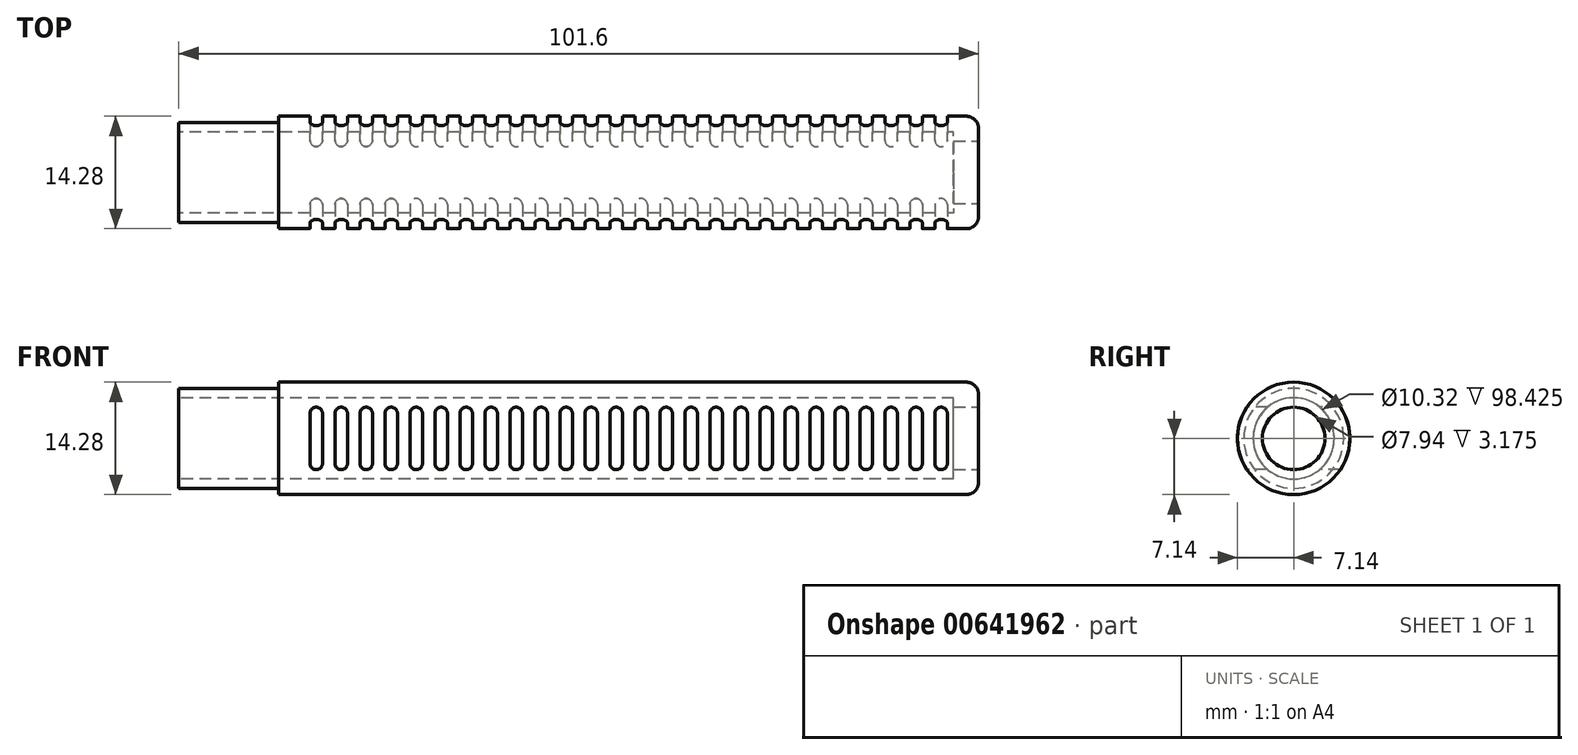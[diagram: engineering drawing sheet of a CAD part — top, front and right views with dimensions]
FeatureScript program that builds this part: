
annotation { "Feature Type Name" : "Feature", "Feature Type Description" : "" }
export const myFeature = defineFeature(function(context is Context, id is Id, definition is map)
    precondition{}
    {
        {
            var Q0;
            Q0=qCreatedBy(makeId("Right.planeOp"),FACE);
            var sketch = newSketch(context, id + "F0", { "sketchPlane" : qUnion([Q0])});
            skCircle(sketch, "E0", {"center": v(0, 0) * mm, "radius": 7.14 * mm});
            skSolve(sketch);
        }
        {
            var Q0;
            Q0=makeQuery(id+"F0.imprint","IMPRINT",FACE,{"disambiguationData":[TD([[makeQuery(id+"F0.imprint","IMPRINT",EDGE,{"derivedFrom":sQuery(id+"F0.wireOp",EDGE,"E0")}),1.0]])]});
            extrude(context, id + "F1", {"entities" : qUnion([Q0]), "depth" : 101.6 * mm, "offsetDistance" : 25.4 * mm});
        }
        {
            var Q0;
            Q0=qCreatedBy(makeId("Right.planeOp"),FACE);
            var sketch = newSketch(context, id + "F2", { "sketchPlane" : qUnion([Q0])});
            skPoint(sketch, "E1", {"position": v(0, 0) * mm});
            skSolve(sketch);
        }
        {
            var Q0;
            Q0=sQuery(id+"F2.wireOp",VERTEX,"E1");
            var Q1;
            Q1=makeQuery(id+"F1.opExtrude","SWEPT_BODY",BODY,{"disambiguationData":[OSD([sQuery(id+"F0.wireOp",EDGE,"E0")])]});
            hole(context, id + "F3", {"style" : HoleStyle.SIMPLE, "endStyle" : HoleEndStyle.THROUGH, "oppositeDirection" : true, "holeDiameter" : 10.32 * mm, "majorDiameter" : 6.35 * mm, "isTappedThrough" : true, "tappedDepth" : 12.7 * mm, "tapClearance" : 3, "locations" : qUnion([Q0]), "scope" : qUnion([Q1])});
        }
        {
            var Q0;
            Q0=qCreatedBy(makeId("Right.planeOp"),FACE);
            var sketch = newSketch(context, id + "F4", { "sketchPlane" : qUnion([Q0])});
            skCircle(sketch, "E2", {"center": v(0, 0) * mm, "radius": 6.35 * mm});
            skCircle(sketch, "E3", {"center": v(0, 0) * mm, "radius": 12.7 * mm});
            skSolve(sketch);
        }
        {
            var Q0;
            Q0=makeQuery(id+"F4.imprint","IMPRINT",FACE,{"disambiguationData":[TD([[makeQuery(id+"F4.imprint","IMPRINT",EDGE,{"derivedFrom":sQuery(id+"F4.wireOp",EDGE,"E2")}),-1.0]])]});
            extrude(context, id + "F5", {"entities" : qUnion([Q0]), "operationType" : NewBodyOperationType.REMOVE, "depth" : 12.7 * mm, "offsetDistance" : 25.4 * mm});
        }
        {
            var Q0;
            Q0=makeQuery(id+"F1.opExtrude","CAP_FACE",FACE,{"disambiguationData":[OSD([sQuery(id+"F0.wireOp",EDGE,"E0")])],"isStart":false});
            var sketch = newSketch(context, id + "F6", { "sketchPlane" : qUnion([Q0])});
            skCircle(sketch, "E4", {"center": v(0, 0) * mm, "radius": 3.97 * mm});
            skCircle(sketch, "E5", {"center": v(0, 0) * mm, "radius": 7.14 * mm});
            skSolve(sketch);
        }
        {
            var Q0;
            Q0=makeQuery(id+"F6.imprint","IMPRINT",FACE,{"disambiguationData":[TD([[makeQuery(id+"F6.imprint","IMPRINT",EDGE,{"derivedFrom":sQuery(id+"F6.wireOp",EDGE,"E4")}),-1.0]])]});
            extrude(context, id + "F7", {"entities" : qUnion([Q0]), "operationType" : NewBodyOperationType.ADD, "oppositeDirection" : true, "depth" : 3.17 * mm, "offsetDistance" : 25.4 * mm});
        }
        {
            var Q0;
            Q0=makeQuery(id+"F1.opExtrude","CAP_EDGE",EDGE,{"disambiguationData":[OSD([sQuery(id+"F0.wireOp",EDGE,"E0")])],"isStart":false});
            fillet(context, id + "F8", {"entities" : qUnion([Q0]), "radius" : 1.59 * mm, "tangentPropagation" : true, "allowEdgeOverflow" : false});
        }
        {
            var Q0;
            Q0=qCreatedBy(makeId("Front.planeOp"),FACE);
            var sketch = newSketch(context, id + "F9", { "sketchPlane" : qUnion([Q0])});
            skLineSegment(sketch, "E6.bottom", {"start": v(96.84, -3.97) * mm, "end": v(96.84, -3.97) * mm});
            skLineSegment(sketch, "E6.top", {"start": v(96.84, 3.97) * mm, "end": v(96.84, 3.97) * mm});
            skLineSegment(sketch, "E6.left", {"start": v(96.04, -3.18) * mm, "end": v(96.04, 3.17) * mm});
            skLineSegment(sketch, "E6.right", {"start": v(97.63, -3.17) * mm, "end": v(97.63, 3.18) * mm});
            skPoint(sketch, "E6.middle", {"position": v(96.84, 0) * mm});
            skPoint(sketch, "E7.visualSharp", {"position": v(96.04, 3.97) * mm});
            skArc(sketch, "E7.filletArc", {"start": v(96.84, 3.97) * mm, "mid": v(96.28, 3.74) * mm, "end": v(96.04, 3.17) * mm});
            skPoint(sketch, "E8.visualSharp", {"position": v(97.63, 3.97) * mm});
            skArc(sketch, "E8.filletArc", {"start": v(97.63, 3.18) * mm, "mid": v(97.4, 3.74) * mm, "end": v(96.84, 3.97) * mm});
            skPoint(sketch, "E9.visualSharp", {"position": v(96.04, -3.97) * mm});
            skArc(sketch, "E9.filletArc", {"start": v(96.04, -3.18) * mm, "mid": v(96.28, -3.74) * mm, "end": v(96.84, -3.97) * mm});
            skPoint(sketch, "E10.visualSharp", {"position": v(97.63, -3.97) * mm});
            skArc(sketch, "E10.filletArc", {"start": v(96.84, -3.97) * mm, "mid": v(97.4, -3.74) * mm, "end": v(97.63, -3.17) * mm});
            skLineSegment(sketch, "E11.1.0.0", {"start": v(93.66, -3.97) * mm, "end": v(93.66, -3.97) * mm});
            skPoint(sketch, "E11.1.0.1", {"position": v(94.46, 3.97) * mm});
            skLineSegment(sketch, "E11.1.0.2", {"start": v(93.66, 3.97) * mm, "end": v(93.66, 3.97) * mm});
            skLineSegment(sketch, "E11.1.0.3", {"start": v(92.87, -3.18) * mm, "end": v(92.87, 3.17) * mm});
            skLineSegment(sketch, "E11.1.0.4", {"start": v(94.46, -3.17) * mm, "end": v(94.46, 3.18) * mm});
            skArc(sketch, "E11.1.0.5", {"start": v(93.66, 3.97) * mm, "mid": v(93.1, 3.74) * mm, "end": v(92.87, 3.17) * mm});
            skArc(sketch, "E11.1.0.6", {"start": v(94.46, 3.18) * mm, "mid": v(94.22, 3.74) * mm, "end": v(93.66, 3.97) * mm});
            skArc(sketch, "E11.1.0.7", {"start": v(93.66, -3.97) * mm, "mid": v(94.22, -3.74) * mm, "end": v(94.46, -3.17) * mm});
            skPoint(sketch, "E11.1.0.8", {"position": v(94.46, -3.97) * mm});
            skArc(sketch, "E11.1.0.9", {"start": v(92.87, -3.18) * mm, "mid": v(93.1, -3.74) * mm, "end": v(93.66, -3.97) * mm});
            skPoint(sketch, "E11.1.0.10", {"position": v(92.87, 3.97) * mm});
            skPoint(sketch, "E11.1.0.11", {"position": v(93.66, 0) * mm});
            skPoint(sketch, "E11.1.0.12", {"position": v(92.87, -3.97) * mm});
            skLineSegment(sketch, "E11.2.0.0", {"start": v(90.49, -3.97) * mm, "end": v(90.49, -3.97) * mm});
            skPoint(sketch, "E11.2.0.1", {"position": v(91.28, 3.97) * mm});
            skLineSegment(sketch, "E11.2.0.2", {"start": v(90.49, 3.97) * mm, "end": v(90.49, 3.97) * mm});
            skLineSegment(sketch, "E11.2.0.3", {"start": v(89.7, -3.18) * mm, "end": v(89.7, 3.17) * mm});
            skLineSegment(sketch, "E11.2.0.4", {"start": v(91.28, -3.17) * mm, "end": v(91.28, 3.18) * mm});
            skArc(sketch, "E11.2.0.5", {"start": v(90.49, 3.97) * mm, "mid": v(89.93, 3.74) * mm, "end": v(89.7, 3.17) * mm});
            skArc(sketch, "E11.2.0.6", {"start": v(91.28, 3.18) * mm, "mid": v(91.05, 3.74) * mm, "end": v(90.49, 3.97) * mm});
            skArc(sketch, "E11.2.0.7", {"start": v(90.49, -3.97) * mm, "mid": v(91.05, -3.74) * mm, "end": v(91.28, -3.17) * mm});
            skPoint(sketch, "E11.2.0.8", {"position": v(91.28, -3.97) * mm});
            skArc(sketch, "E11.2.0.9", {"start": v(89.7, -3.18) * mm, "mid": v(89.93, -3.74) * mm, "end": v(90.49, -3.97) * mm});
            skPoint(sketch, "E11.2.0.10", {"position": v(89.7, 3.97) * mm});
            skPoint(sketch, "E11.2.0.11", {"position": v(90.49, 0) * mm});
            skPoint(sketch, "E11.2.0.12", {"position": v(89.7, -3.97) * mm});
            skLineSegment(sketch, "E11.3.0.0", {"start": v(87.31, -3.97) * mm, "end": v(87.31, -3.97) * mm});
            skPoint(sketch, "E11.3.0.1", {"position": v(88.1, 3.97) * mm});
            skLineSegment(sketch, "E11.3.0.2", {"start": v(87.31, 3.97) * mm, "end": v(87.31, 3.97) * mm});
            skLineSegment(sketch, "E11.3.0.3", {"start": v(86.52, -3.18) * mm, "end": v(86.52, 3.17) * mm});
            skLineSegment(sketch, "E11.3.0.4", {"start": v(88.1, -3.17) * mm, "end": v(88.1, 3.18) * mm});
            skArc(sketch, "E11.3.0.5", {"start": v(87.31, 3.97) * mm, "mid": v(86.75, 3.74) * mm, "end": v(86.52, 3.17) * mm});
            skArc(sketch, "E11.3.0.6", {"start": v(88.1, 3.18) * mm, "mid": v(87.87, 3.74) * mm, "end": v(87.31, 3.97) * mm});
            skArc(sketch, "E11.3.0.7", {"start": v(87.31, -3.97) * mm, "mid": v(87.87, -3.74) * mm, "end": v(88.1, -3.17) * mm});
            skPoint(sketch, "E11.3.0.8", {"position": v(88.1, -3.97) * mm});
            skArc(sketch, "E11.3.0.9", {"start": v(86.52, -3.18) * mm, "mid": v(86.75, -3.74) * mm, "end": v(87.31, -3.97) * mm});
            skPoint(sketch, "E11.3.0.10", {"position": v(86.52, 3.97) * mm});
            skPoint(sketch, "E11.3.0.11", {"position": v(87.31, 0) * mm});
            skPoint(sketch, "E11.3.0.12", {"position": v(86.52, -3.97) * mm});
            skLineSegment(sketch, "E11.4.0.0", {"start": v(84.14, -3.97) * mm, "end": v(84.14, -3.97) * mm});
            skPoint(sketch, "E11.4.0.1", {"position": v(84.93, 3.97) * mm});
            skLineSegment(sketch, "E11.4.0.2", {"start": v(84.14, 3.97) * mm, "end": v(84.14, 3.97) * mm});
            skLineSegment(sketch, "E11.4.0.3", {"start": v(83.34, -3.18) * mm, "end": v(83.34, 3.17) * mm});
            skLineSegment(sketch, "E11.4.0.4", {"start": v(84.93, -3.17) * mm, "end": v(84.93, 3.18) * mm});
            skArc(sketch, "E11.4.0.5", {"start": v(84.14, 3.97) * mm, "mid": v(83.58, 3.74) * mm, "end": v(83.34, 3.17) * mm});
            skArc(sketch, "E11.4.0.6", {"start": v(84.93, 3.18) * mm, "mid": v(84.7, 3.74) * mm, "end": v(84.14, 3.97) * mm});
            skArc(sketch, "E11.4.0.7", {"start": v(84.14, -3.97) * mm, "mid": v(84.7, -3.74) * mm, "end": v(84.93, -3.17) * mm});
            skPoint(sketch, "E11.4.0.8", {"position": v(84.93, -3.97) * mm});
            skArc(sketch, "E11.4.0.9", {"start": v(83.34, -3.18) * mm, "mid": v(83.58, -3.74) * mm, "end": v(84.14, -3.97) * mm});
            skPoint(sketch, "E11.4.0.10", {"position": v(83.34, 3.97) * mm});
            skPoint(sketch, "E11.4.0.11", {"position": v(84.14, 0) * mm});
            skPoint(sketch, "E11.4.0.12", {"position": v(83.34, -3.97) * mm});
            skLineSegment(sketch, "E11.5.0.0", {"start": v(80.96, -3.97) * mm, "end": v(80.96, -3.97) * mm});
            skPoint(sketch, "E11.5.0.1", {"position": v(81.76, 3.97) * mm});
            skLineSegment(sketch, "E11.5.0.2", {"start": v(80.96, 3.97) * mm, "end": v(80.96, 3.97) * mm});
            skLineSegment(sketch, "E11.5.0.3", {"start": v(80.17, -3.18) * mm, "end": v(80.17, 3.17) * mm});
            skLineSegment(sketch, "E11.5.0.4", {"start": v(81.76, -3.17) * mm, "end": v(81.76, 3.18) * mm});
            skArc(sketch, "E11.5.0.5", {"start": v(80.96, 3.97) * mm, "mid": v(80.4, 3.74) * mm, "end": v(80.17, 3.17) * mm});
            skArc(sketch, "E11.5.0.6", {"start": v(81.76, 3.18) * mm, "mid": v(81.52, 3.74) * mm, "end": v(80.96, 3.97) * mm});
            skArc(sketch, "E11.5.0.7", {"start": v(80.96, -3.97) * mm, "mid": v(81.52, -3.74) * mm, "end": v(81.76, -3.17) * mm});
            skPoint(sketch, "E11.5.0.8", {"position": v(81.76, -3.97) * mm});
            skArc(sketch, "E11.5.0.9", {"start": v(80.17, -3.18) * mm, "mid": v(80.4, -3.74) * mm, "end": v(80.96, -3.97) * mm});
            skPoint(sketch, "E11.5.0.10", {"position": v(80.17, 3.97) * mm});
            skPoint(sketch, "E11.5.0.11", {"position": v(80.96, 0) * mm});
            skPoint(sketch, "E11.5.0.12", {"position": v(80.17, -3.97) * mm});
            skLineSegment(sketch, "E11.6.0.0", {"start": v(77.79, -3.97) * mm, "end": v(77.79, -3.97) * mm});
            skPoint(sketch, "E11.6.0.1", {"position": v(78.58, 3.97) * mm});
            skLineSegment(sketch, "E11.6.0.2", {"start": v(77.79, 3.97) * mm, "end": v(77.79, 3.97) * mm});
            skLineSegment(sketch, "E11.6.0.3", {"start": v(77, -3.18) * mm, "end": v(77, 3.17) * mm});
            skLineSegment(sketch, "E11.6.0.4", {"start": v(78.58, -3.17) * mm, "end": v(78.58, 3.18) * mm});
            skArc(sketch, "E11.6.0.5", {"start": v(77.79, 3.97) * mm, "mid": v(77.23, 3.74) * mm, "end": v(77, 3.17) * mm});
            skArc(sketch, "E11.6.0.6", {"start": v(78.58, 3.18) * mm, "mid": v(78.35, 3.74) * mm, "end": v(77.79, 3.97) * mm});
            skArc(sketch, "E11.6.0.7", {"start": v(77.79, -3.97) * mm, "mid": v(78.35, -3.74) * mm, "end": v(78.58, -3.17) * mm});
            skPoint(sketch, "E11.6.0.8", {"position": v(78.58, -3.97) * mm});
            skArc(sketch, "E11.6.0.9", {"start": v(77, -3.18) * mm, "mid": v(77.23, -3.74) * mm, "end": v(77.79, -3.97) * mm});
            skPoint(sketch, "E11.6.0.10", {"position": v(77, 3.97) * mm});
            skPoint(sketch, "E11.6.0.11", {"position": v(77.79, 0) * mm});
            skPoint(sketch, "E11.6.0.12", {"position": v(77, -3.97) * mm});
            skLineSegment(sketch, "E11.7.0.0", {"start": v(74.61, -3.97) * mm, "end": v(74.61, -3.97) * mm});
            skPoint(sketch, "E11.7.0.1", {"position": v(75.4, 3.97) * mm});
            skLineSegment(sketch, "E11.7.0.2", {"start": v(74.61, 3.97) * mm, "end": v(74.61, 3.97) * mm});
            skLineSegment(sketch, "E11.7.0.3", {"start": v(73.82, -3.18) * mm, "end": v(73.82, 3.17) * mm});
            skLineSegment(sketch, "E11.7.0.4", {"start": v(75.4, -3.17) * mm, "end": v(75.4, 3.18) * mm});
            skArc(sketch, "E11.7.0.5", {"start": v(74.61, 3.97) * mm, "mid": v(74.05, 3.74) * mm, "end": v(73.82, 3.17) * mm});
            skArc(sketch, "E11.7.0.6", {"start": v(75.4, 3.18) * mm, "mid": v(75.17, 3.74) * mm, "end": v(74.61, 3.97) * mm});
            skArc(sketch, "E11.7.0.7", {"start": v(74.61, -3.97) * mm, "mid": v(75.17, -3.74) * mm, "end": v(75.4, -3.17) * mm});
            skPoint(sketch, "E11.7.0.8", {"position": v(75.4, -3.97) * mm});
            skArc(sketch, "E11.7.0.9", {"start": v(73.82, -3.18) * mm, "mid": v(74.05, -3.74) * mm, "end": v(74.61, -3.97) * mm});
            skPoint(sketch, "E11.7.0.10", {"position": v(73.82, 3.97) * mm});
            skPoint(sketch, "E11.7.0.11", {"position": v(74.61, 0) * mm});
            skPoint(sketch, "E11.7.0.12", {"position": v(73.82, -3.97) * mm});
            skLineSegment(sketch, "E11.8.0.0", {"start": v(71.44, -3.97) * mm, "end": v(71.44, -3.97) * mm});
            skPoint(sketch, "E11.8.0.1", {"position": v(72.23, 3.97) * mm});
            skLineSegment(sketch, "E11.8.0.2", {"start": v(71.44, 3.97) * mm, "end": v(71.44, 3.97) * mm});
            skLineSegment(sketch, "E11.8.0.3", {"start": v(70.64, -3.18) * mm, "end": v(70.64, 3.17) * mm});
            skLineSegment(sketch, "E11.8.0.4", {"start": v(72.23, -3.17) * mm, "end": v(72.23, 3.18) * mm});
            skArc(sketch, "E11.8.0.5", {"start": v(71.44, 3.97) * mm, "mid": v(70.88, 3.74) * mm, "end": v(70.64, 3.17) * mm});
            skArc(sketch, "E11.8.0.6", {"start": v(72.23, 3.18) * mm, "mid": v(72, 3.74) * mm, "end": v(71.44, 3.97) * mm});
            skArc(sketch, "E11.8.0.7", {"start": v(71.44, -3.97) * mm, "mid": v(72, -3.74) * mm, "end": v(72.23, -3.17) * mm});
            skPoint(sketch, "E11.8.0.8", {"position": v(72.23, -3.97) * mm});
            skArc(sketch, "E11.8.0.9", {"start": v(70.64, -3.18) * mm, "mid": v(70.88, -3.74) * mm, "end": v(71.44, -3.97) * mm});
            skPoint(sketch, "E11.8.0.10", {"position": v(70.64, 3.97) * mm});
            skPoint(sketch, "E11.8.0.11", {"position": v(71.44, 0) * mm});
            skPoint(sketch, "E11.8.0.12", {"position": v(70.64, -3.97) * mm});
            skLineSegment(sketch, "E11.9.0.0", {"start": v(68.26, -3.97) * mm, "end": v(68.26, -3.97) * mm});
            skPoint(sketch, "E11.9.0.1", {"position": v(69.06, 3.97) * mm});
            skLineSegment(sketch, "E11.9.0.2", {"start": v(68.26, 3.97) * mm, "end": v(68.26, 3.97) * mm});
            skLineSegment(sketch, "E11.9.0.3", {"start": v(67.47, -3.18) * mm, "end": v(67.47, 3.17) * mm});
            skLineSegment(sketch, "E11.9.0.4", {"start": v(69.06, -3.17) * mm, "end": v(69.06, 3.17) * mm});
            skArc(sketch, "E11.9.0.5", {"start": v(68.26, 3.97) * mm, "mid": v(67.7, 3.74) * mm, "end": v(67.47, 3.17) * mm});
            skArc(sketch, "E11.9.0.6", {"start": v(69.06, 3.17) * mm, "mid": v(68.82, 3.74) * mm, "end": v(68.26, 3.97) * mm});
            skArc(sketch, "E11.9.0.7", {"start": v(68.26, -3.97) * mm, "mid": v(68.82, -3.74) * mm, "end": v(69.06, -3.17) * mm});
            skPoint(sketch, "E11.9.0.8", {"position": v(69.06, -3.97) * mm});
            skArc(sketch, "E11.9.0.9", {"start": v(67.47, -3.18) * mm, "mid": v(67.7, -3.74) * mm, "end": v(68.26, -3.97) * mm});
            skPoint(sketch, "E11.9.0.10", {"position": v(67.47, 3.97) * mm});
            skPoint(sketch, "E11.9.0.11", {"position": v(68.26, 0) * mm});
            skPoint(sketch, "E11.9.0.12", {"position": v(67.47, -3.97) * mm});
            skLineSegment(sketch, "E11.10.0.0", {"start": v(65.09, -3.97) * mm, "end": v(65.09, -3.97) * mm});
            skPoint(sketch, "E11.10.0.1", {"position": v(65.88, 3.97) * mm});
            skLineSegment(sketch, "E11.10.0.2", {"start": v(65.09, 3.97) * mm, "end": v(65.09, 3.97) * mm});
            skLineSegment(sketch, "E11.10.0.3", {"start": v(64.3, -3.18) * mm, "end": v(64.3, 3.17) * mm});
            skLineSegment(sketch, "E11.10.0.4", {"start": v(65.88, -3.17) * mm, "end": v(65.88, 3.17) * mm});
            skArc(sketch, "E11.10.0.5", {"start": v(65.09, 3.97) * mm, "mid": v(64.53, 3.74) * mm, "end": v(64.3, 3.17) * mm});
            skArc(sketch, "E11.10.0.6", {"start": v(65.88, 3.17) * mm, "mid": v(65.65, 3.74) * mm, "end": v(65.09, 3.97) * mm});
            skArc(sketch, "E11.10.0.7", {"start": v(65.09, -3.97) * mm, "mid": v(65.65, -3.74) * mm, "end": v(65.88, -3.17) * mm});
            skPoint(sketch, "E11.10.0.8", {"position": v(65.88, -3.97) * mm});
            skArc(sketch, "E11.10.0.9", {"start": v(64.3, -3.18) * mm, "mid": v(64.53, -3.74) * mm, "end": v(65.09, -3.97) * mm});
            skPoint(sketch, "E11.10.0.10", {"position": v(64.3, 3.97) * mm});
            skPoint(sketch, "E11.10.0.11", {"position": v(65.09, 0) * mm});
            skPoint(sketch, "E11.10.0.12", {"position": v(64.3, -3.97) * mm});
            skLineSegment(sketch, "E11.11.0.0", {"start": v(61.91, -3.97) * mm, "end": v(61.91, -3.97) * mm});
            skPoint(sketch, "E11.11.0.1", {"position": v(62.7, 3.97) * mm});
            skLineSegment(sketch, "E11.11.0.2", {"start": v(61.91, 3.97) * mm, "end": v(61.91, 3.97) * mm});
            skLineSegment(sketch, "E11.11.0.3", {"start": v(61.12, -3.18) * mm, "end": v(61.12, 3.17) * mm});
            skLineSegment(sketch, "E11.11.0.4", {"start": v(62.7, -3.17) * mm, "end": v(62.7, 3.17) * mm});
            skArc(sketch, "E11.11.0.5", {"start": v(61.91, 3.97) * mm, "mid": v(61.35, 3.74) * mm, "end": v(61.12, 3.17) * mm});
            skArc(sketch, "E11.11.0.6", {"start": v(62.7, 3.17) * mm, "mid": v(62.47, 3.74) * mm, "end": v(61.91, 3.97) * mm});
            skArc(sketch, "E11.11.0.7", {"start": v(61.91, -3.97) * mm, "mid": v(62.47, -3.74) * mm, "end": v(62.7, -3.17) * mm});
            skPoint(sketch, "E11.11.0.8", {"position": v(62.7, -3.97) * mm});
            skArc(sketch, "E11.11.0.9", {"start": v(61.12, -3.18) * mm, "mid": v(61.35, -3.74) * mm, "end": v(61.91, -3.97) * mm});
            skPoint(sketch, "E11.11.0.10", {"position": v(61.12, 3.97) * mm});
            skPoint(sketch, "E11.11.0.11", {"position": v(61.91, 0) * mm});
            skPoint(sketch, "E11.11.0.12", {"position": v(61.12, -3.97) * mm});
            skLineSegment(sketch, "E11.direction1", {"start": v(96.04, -3.97) * mm, "end": v(92.87, -3.97) * mm, "construction": true});
            skLineSegment(sketch, "E12.0.12.0", {"start": v(58.74, -3.97) * mm, "end": v(58.74, -3.97) * mm});
            skPoint(sketch, "E12.3.12.0", {"position": v(59.53, 3.97) * mm});
            skLineSegment(sketch, "E12.4.12.0", {"start": v(58.74, 3.97) * mm, "end": v(58.74, 3.97) * mm});
            skLineSegment(sketch, "E12.7.12.0", {"start": v(57.94, -3.18) * mm, "end": v(57.94, 3.17) * mm});
            skLineSegment(sketch, "E12.10.12.0", {"start": v(59.53, -3.18) * mm, "end": v(59.53, 3.17) * mm});
            skArc(sketch, "E12.13.12.0", {"start": v(58.74, 3.97) * mm, "mid": v(58.18, 3.74) * mm, "end": v(57.94, 3.17) * mm});
            skArc(sketch, "E12.17.12.0", {"start": v(59.53, 3.17) * mm, "mid": v(59.3, 3.74) * mm, "end": v(58.74, 3.97) * mm});
            skArc(sketch, "E12.21.12.0", {"start": v(58.74, -3.97) * mm, "mid": v(59.3, -3.74) * mm, "end": v(59.53, -3.18) * mm});
            skPoint(sketch, "E12.25.12.0", {"position": v(59.53, -3.97) * mm});
            skArc(sketch, "E12.26.12.0", {"start": v(57.94, -3.18) * mm, "mid": v(58.18, -3.74) * mm, "end": v(58.74, -3.97) * mm});
            skPoint(sketch, "E12.30.12.0", {"position": v(57.94, 3.97) * mm});
            skPoint(sketch, "E12.31.12.0", {"position": v(58.74, 0) * mm});
            skPoint(sketch, "E12.32.12.0", {"position": v(57.94, -3.97) * mm});
            skLineSegment(sketch, "E12.0.13.0", {"start": v(55.56, -3.97) * mm, "end": v(55.56, -3.97) * mm});
            skPoint(sketch, "E12.3.13.0", {"position": v(56.36, 3.97) * mm});
            skLineSegment(sketch, "E12.4.13.0", {"start": v(55.56, 3.97) * mm, "end": v(55.56, 3.97) * mm});
            skLineSegment(sketch, "E12.7.13.0", {"start": v(54.77, -3.18) * mm, "end": v(54.77, 3.17) * mm});
            skLineSegment(sketch, "E12.10.13.0", {"start": v(56.36, -3.18) * mm, "end": v(56.36, 3.17) * mm});
            skArc(sketch, "E12.13.13.0", {"start": v(55.56, 3.97) * mm, "mid": v(55, 3.74) * mm, "end": v(54.77, 3.17) * mm});
            skArc(sketch, "E12.17.13.0", {"start": v(56.36, 3.17) * mm, "mid": v(56.12, 3.74) * mm, "end": v(55.56, 3.97) * mm});
            skArc(sketch, "E12.21.13.0", {"start": v(55.56, -3.97) * mm, "mid": v(56.12, -3.74) * mm, "end": v(56.36, -3.18) * mm});
            skPoint(sketch, "E12.25.13.0", {"position": v(56.36, -3.97) * mm});
            skArc(sketch, "E12.26.13.0", {"start": v(54.77, -3.18) * mm, "mid": v(55, -3.74) * mm, "end": v(55.56, -3.97) * mm});
            skPoint(sketch, "E12.30.13.0", {"position": v(54.77, 3.97) * mm});
            skPoint(sketch, "E12.31.13.0", {"position": v(55.56, 0) * mm});
            skPoint(sketch, "E12.32.13.0", {"position": v(54.77, -3.97) * mm});
            skLineSegment(sketch, "E12.0.14.0", {"start": v(52.39, -3.97) * mm, "end": v(52.39, -3.97) * mm});
            skPoint(sketch, "E12.3.14.0", {"position": v(53.18, 3.97) * mm});
            skLineSegment(sketch, "E12.4.14.0", {"start": v(52.39, 3.97) * mm, "end": v(52.39, 3.97) * mm});
            skLineSegment(sketch, "E12.7.14.0", {"start": v(51.6, -3.18) * mm, "end": v(51.6, 3.17) * mm});
            skLineSegment(sketch, "E12.10.14.0", {"start": v(53.18, -3.18) * mm, "end": v(53.18, 3.17) * mm});
            skArc(sketch, "E12.13.14.0", {"start": v(52.39, 3.97) * mm, "mid": v(51.83, 3.74) * mm, "end": v(51.6, 3.17) * mm});
            skArc(sketch, "E12.17.14.0", {"start": v(53.18, 3.17) * mm, "mid": v(52.95, 3.74) * mm, "end": v(52.39, 3.97) * mm});
            skArc(sketch, "E12.21.14.0", {"start": v(52.39, -3.97) * mm, "mid": v(52.95, -3.74) * mm, "end": v(53.18, -3.18) * mm});
            skPoint(sketch, "E12.25.14.0", {"position": v(53.18, -3.97) * mm});
            skArc(sketch, "E12.26.14.0", {"start": v(51.6, -3.18) * mm, "mid": v(51.83, -3.74) * mm, "end": v(52.39, -3.97) * mm});
            skPoint(sketch, "E12.30.14.0", {"position": v(51.6, 3.97) * mm});
            skPoint(sketch, "E12.31.14.0", {"position": v(52.39, 0) * mm});
            skPoint(sketch, "E12.32.14.0", {"position": v(51.6, -3.97) * mm});
            skLineSegment(sketch, "E12.0.15.0", {"start": v(49.21, -3.97) * mm, "end": v(49.21, -3.97) * mm});
            skPoint(sketch, "E12.3.15.0", {"position": v(50, 3.97) * mm});
            skLineSegment(sketch, "E12.4.15.0", {"start": v(49.21, 3.97) * mm, "end": v(49.21, 3.97) * mm});
            skLineSegment(sketch, "E12.7.15.0", {"start": v(48.42, -3.18) * mm, "end": v(48.42, 3.17) * mm});
            skLineSegment(sketch, "E12.10.15.0", {"start": v(50, -3.18) * mm, "end": v(50, 3.17) * mm});
            skArc(sketch, "E12.13.15.0", {"start": v(49.21, 3.97) * mm, "mid": v(48.65, 3.74) * mm, "end": v(48.42, 3.17) * mm});
            skArc(sketch, "E12.17.15.0", {"start": v(50, 3.17) * mm, "mid": v(49.77, 3.74) * mm, "end": v(49.21, 3.97) * mm});
            skArc(sketch, "E12.21.15.0", {"start": v(49.21, -3.97) * mm, "mid": v(49.77, -3.74) * mm, "end": v(50, -3.18) * mm});
            skPoint(sketch, "E12.25.15.0", {"position": v(50, -3.97) * mm});
            skArc(sketch, "E12.26.15.0", {"start": v(48.42, -3.18) * mm, "mid": v(48.65, -3.74) * mm, "end": v(49.21, -3.97) * mm});
            skPoint(sketch, "E12.30.15.0", {"position": v(48.42, 3.97) * mm});
            skPoint(sketch, "E12.31.15.0", {"position": v(49.21, 0) * mm});
            skPoint(sketch, "E12.32.15.0", {"position": v(48.42, -3.97) * mm});
            skLineSegment(sketch, "E13.0.16.0", {"start": v(46.04, -3.97) * mm, "end": v(46.04, -3.97) * mm});
            skPoint(sketch, "E13.3.16.0", {"position": v(46.83, 3.97) * mm});
            skLineSegment(sketch, "E13.4.16.0", {"start": v(46.04, 3.97) * mm, "end": v(46.04, 3.97) * mm});
            skLineSegment(sketch, "E13.7.16.0", {"start": v(45.24, -3.18) * mm, "end": v(45.24, 3.17) * mm});
            skLineSegment(sketch, "E13.10.16.0", {"start": v(46.83, -3.18) * mm, "end": v(46.83, 3.17) * mm});
            skArc(sketch, "E13.13.16.0", {"start": v(46.04, 3.97) * mm, "mid": v(45.48, 3.74) * mm, "end": v(45.24, 3.17) * mm});
            skArc(sketch, "E13.17.16.0", {"start": v(46.83, 3.17) * mm, "mid": v(46.6, 3.74) * mm, "end": v(46.04, 3.97) * mm});
            skArc(sketch, "E13.21.16.0", {"start": v(46.04, -3.97) * mm, "mid": v(46.6, -3.74) * mm, "end": v(46.83, -3.18) * mm});
            skPoint(sketch, "E13.25.16.0", {"position": v(46.83, -3.97) * mm});
            skArc(sketch, "E13.26.16.0", {"start": v(45.24, -3.18) * mm, "mid": v(45.48, -3.74) * mm, "end": v(46.04, -3.97) * mm});
            skPoint(sketch, "E13.30.16.0", {"position": v(45.24, 3.97) * mm});
            skPoint(sketch, "E13.31.16.0", {"position": v(46.04, 0) * mm});
            skPoint(sketch, "E13.32.16.0", {"position": v(45.24, -3.97) * mm});
            skLineSegment(sketch, "E13.0.17.0", {"start": v(42.86, -3.97) * mm, "end": v(42.86, -3.97) * mm});
            skPoint(sketch, "E13.3.17.0", {"position": v(43.66, 3.97) * mm});
            skLineSegment(sketch, "E13.4.17.0", {"start": v(42.86, 3.97) * mm, "end": v(42.86, 3.97) * mm});
            skLineSegment(sketch, "E13.7.17.0", {"start": v(42.07, -3.18) * mm, "end": v(42.07, 3.17) * mm});
            skLineSegment(sketch, "E13.10.17.0", {"start": v(43.66, -3.18) * mm, "end": v(43.66, 3.17) * mm});
            skArc(sketch, "E13.13.17.0", {"start": v(42.86, 3.97) * mm, "mid": v(42.3, 3.74) * mm, "end": v(42.07, 3.17) * mm});
            skArc(sketch, "E13.17.17.0", {"start": v(43.66, 3.17) * mm, "mid": v(43.42, 3.74) * mm, "end": v(42.86, 3.97) * mm});
            skArc(sketch, "E13.21.17.0", {"start": v(42.86, -3.97) * mm, "mid": v(43.42, -3.74) * mm, "end": v(43.66, -3.18) * mm});
            skPoint(sketch, "E13.25.17.0", {"position": v(43.66, -3.97) * mm});
            skArc(sketch, "E13.26.17.0", {"start": v(42.07, -3.18) * mm, "mid": v(42.3, -3.74) * mm, "end": v(42.86, -3.97) * mm});
            skPoint(sketch, "E13.30.17.0", {"position": v(42.07, 3.97) * mm});
            skPoint(sketch, "E13.31.17.0", {"position": v(42.86, 0) * mm});
            skPoint(sketch, "E13.32.17.0", {"position": v(42.07, -3.97) * mm});
            skLineSegment(sketch, "E13.0.18.0", {"start": v(39.69, -3.97) * mm, "end": v(39.69, -3.97) * mm});
            skPoint(sketch, "E13.3.18.0", {"position": v(40.48, 3.97) * mm});
            skLineSegment(sketch, "E13.4.18.0", {"start": v(39.69, 3.97) * mm, "end": v(39.69, 3.97) * mm});
            skLineSegment(sketch, "E13.7.18.0", {"start": v(38.9, -3.18) * mm, "end": v(38.9, 3.17) * mm});
            skLineSegment(sketch, "E13.10.18.0", {"start": v(40.48, -3.18) * mm, "end": v(40.48, 3.17) * mm});
            skArc(sketch, "E13.13.18.0", {"start": v(39.69, 3.97) * mm, "mid": v(39.13, 3.74) * mm, "end": v(38.9, 3.17) * mm});
            skArc(sketch, "E13.17.18.0", {"start": v(40.48, 3.17) * mm, "mid": v(40.25, 3.74) * mm, "end": v(39.69, 3.97) * mm});
            skArc(sketch, "E13.21.18.0", {"start": v(39.69, -3.97) * mm, "mid": v(40.25, -3.74) * mm, "end": v(40.48, -3.18) * mm});
            skPoint(sketch, "E13.25.18.0", {"position": v(40.48, -3.97) * mm});
            skArc(sketch, "E13.26.18.0", {"start": v(38.9, -3.18) * mm, "mid": v(39.13, -3.74) * mm, "end": v(39.69, -3.97) * mm});
            skPoint(sketch, "E13.30.18.0", {"position": v(38.9, 3.97) * mm});
            skPoint(sketch, "E13.31.18.0", {"position": v(39.69, 0) * mm});
            skPoint(sketch, "E13.32.18.0", {"position": v(38.9, -3.97) * mm});
            skLineSegment(sketch, "E13.0.19.0", {"start": v(36.51, -3.97) * mm, "end": v(36.51, -3.97) * mm});
            skPoint(sketch, "E13.3.19.0", {"position": v(37.3, 3.97) * mm});
            skLineSegment(sketch, "E13.4.19.0", {"start": v(36.51, 3.97) * mm, "end": v(36.51, 3.97) * mm});
            skLineSegment(sketch, "E13.7.19.0", {"start": v(35.72, -3.18) * mm, "end": v(35.72, 3.17) * mm});
            skLineSegment(sketch, "E13.10.19.0", {"start": v(37.3, -3.18) * mm, "end": v(37.3, 3.17) * mm});
            skArc(sketch, "E13.13.19.0", {"start": v(36.51, 3.97) * mm, "mid": v(35.95, 3.74) * mm, "end": v(35.72, 3.17) * mm});
            skArc(sketch, "E13.17.19.0", {"start": v(37.3, 3.17) * mm, "mid": v(37.07, 3.74) * mm, "end": v(36.51, 3.97) * mm});
            skArc(sketch, "E13.21.19.0", {"start": v(36.51, -3.97) * mm, "mid": v(37.07, -3.74) * mm, "end": v(37.3, -3.18) * mm});
            skPoint(sketch, "E13.25.19.0", {"position": v(37.3, -3.97) * mm});
            skArc(sketch, "E13.26.19.0", {"start": v(35.72, -3.18) * mm, "mid": v(35.95, -3.74) * mm, "end": v(36.51, -3.97) * mm});
            skPoint(sketch, "E13.30.19.0", {"position": v(35.72, 3.97) * mm});
            skPoint(sketch, "E13.31.19.0", {"position": v(36.51, 0) * mm});
            skPoint(sketch, "E13.32.19.0", {"position": v(35.72, -3.97) * mm});
            skLineSegment(sketch, "E13.0.20.0", {"start": v(33.34, -3.97) * mm, "end": v(33.34, -3.97) * mm});
            skPoint(sketch, "E13.3.20.0", {"position": v(34.13, 3.97) * mm});
            skLineSegment(sketch, "E13.4.20.0", {"start": v(33.34, 3.97) * mm, "end": v(33.34, 3.97) * mm});
            skLineSegment(sketch, "E13.7.20.0", {"start": v(32.54, -3.18) * mm, "end": v(32.54, 3.17) * mm});
            skLineSegment(sketch, "E13.10.20.0", {"start": v(34.13, -3.18) * mm, "end": v(34.13, 3.17) * mm});
            skArc(sketch, "E13.13.20.0", {"start": v(33.34, 3.97) * mm, "mid": v(32.78, 3.74) * mm, "end": v(32.54, 3.17) * mm});
            skArc(sketch, "E13.17.20.0", {"start": v(34.13, 3.17) * mm, "mid": v(33.9, 3.74) * mm, "end": v(33.34, 3.97) * mm});
            skArc(sketch, "E13.21.20.0", {"start": v(33.34, -3.97) * mm, "mid": v(33.9, -3.74) * mm, "end": v(34.13, -3.18) * mm});
            skPoint(sketch, "E13.25.20.0", {"position": v(34.13, -3.97) * mm});
            skArc(sketch, "E13.26.20.0", {"start": v(32.54, -3.18) * mm, "mid": v(32.78, -3.74) * mm, "end": v(33.34, -3.97) * mm});
            skPoint(sketch, "E13.30.20.0", {"position": v(32.54, 3.97) * mm});
            skPoint(sketch, "E13.31.20.0", {"position": v(33.34, 0) * mm});
            skPoint(sketch, "E13.32.20.0", {"position": v(32.54, -3.97) * mm});
            skLineSegment(sketch, "E13.0.21.0", {"start": v(30.16, -3.97) * mm, "end": v(30.16, -3.97) * mm});
            skPoint(sketch, "E13.3.21.0", {"position": v(30.96, 3.97) * mm});
            skLineSegment(sketch, "E13.4.21.0", {"start": v(30.16, 3.97) * mm, "end": v(30.16, 3.97) * mm});
            skLineSegment(sketch, "E13.7.21.0", {"start": v(29.37, -3.18) * mm, "end": v(29.37, 3.17) * mm});
            skLineSegment(sketch, "E13.10.21.0", {"start": v(30.96, -3.18) * mm, "end": v(30.96, 3.17) * mm});
            skArc(sketch, "E13.13.21.0", {"start": v(30.16, 3.97) * mm, "mid": v(29.6, 3.74) * mm, "end": v(29.37, 3.17) * mm});
            skArc(sketch, "E13.17.21.0", {"start": v(30.96, 3.17) * mm, "mid": v(30.72, 3.74) * mm, "end": v(30.16, 3.97) * mm});
            skArc(sketch, "E13.21.21.0", {"start": v(30.16, -3.97) * mm, "mid": v(30.72, -3.74) * mm, "end": v(30.96, -3.18) * mm});
            skPoint(sketch, "E13.25.21.0", {"position": v(30.96, -3.97) * mm});
            skArc(sketch, "E13.26.21.0", {"start": v(29.37, -3.18) * mm, "mid": v(29.6, -3.74) * mm, "end": v(30.16, -3.97) * mm});
            skPoint(sketch, "E13.30.21.0", {"position": v(29.37, 3.97) * mm});
            skPoint(sketch, "E13.31.21.0", {"position": v(30.16, 0) * mm});
            skPoint(sketch, "E13.32.21.0", {"position": v(29.37, -3.97) * mm});
            skLineSegment(sketch, "E13.0.22.0", {"start": v(26.99, -3.97) * mm, "end": v(26.99, -3.97) * mm});
            skPoint(sketch, "E13.3.22.0", {"position": v(27.78, 3.97) * mm});
            skLineSegment(sketch, "E13.4.22.0", {"start": v(26.99, 3.97) * mm, "end": v(26.99, 3.97) * mm});
            skLineSegment(sketch, "E13.7.22.0", {"start": v(26.2, -3.18) * mm, "end": v(26.2, 3.17) * mm});
            skLineSegment(sketch, "E13.10.22.0", {"start": v(27.78, -3.18) * mm, "end": v(27.78, 3.17) * mm});
            skArc(sketch, "E13.13.22.0", {"start": v(26.99, 3.97) * mm, "mid": v(26.43, 3.74) * mm, "end": v(26.2, 3.17) * mm});
            skArc(sketch, "E13.17.22.0", {"start": v(27.78, 3.17) * mm, "mid": v(27.55, 3.74) * mm, "end": v(26.99, 3.97) * mm});
            skArc(sketch, "E13.21.22.0", {"start": v(26.99, -3.97) * mm, "mid": v(27.55, -3.74) * mm, "end": v(27.78, -3.18) * mm});
            skPoint(sketch, "E13.25.22.0", {"position": v(27.78, -3.97) * mm});
            skArc(sketch, "E13.26.22.0", {"start": v(26.2, -3.18) * mm, "mid": v(26.43, -3.74) * mm, "end": v(26.99, -3.97) * mm});
            skPoint(sketch, "E13.30.22.0", {"position": v(26.2, 3.97) * mm});
            skPoint(sketch, "E13.31.22.0", {"position": v(26.99, 0) * mm});
            skPoint(sketch, "E13.32.22.0", {"position": v(26.2, -3.97) * mm});
            skLineSegment(sketch, "E13.0.23.0", {"start": v(23.81, -3.97) * mm, "end": v(23.81, -3.97) * mm});
            skPoint(sketch, "E13.3.23.0", {"position": v(24.6, 3.97) * mm});
            skLineSegment(sketch, "E13.4.23.0", {"start": v(23.81, 3.97) * mm, "end": v(23.81, 3.97) * mm});
            skLineSegment(sketch, "E13.7.23.0", {"start": v(23.02, -3.18) * mm, "end": v(23.02, 3.17) * mm});
            skLineSegment(sketch, "E13.10.23.0", {"start": v(24.6, -3.18) * mm, "end": v(24.6, 3.17) * mm});
            skArc(sketch, "E13.13.23.0", {"start": v(23.81, 3.97) * mm, "mid": v(23.25, 3.74) * mm, "end": v(23.02, 3.17) * mm});
            skArc(sketch, "E13.17.23.0", {"start": v(24.6, 3.17) * mm, "mid": v(24.37, 3.74) * mm, "end": v(23.81, 3.97) * mm});
            skArc(sketch, "E13.21.23.0", {"start": v(23.81, -3.97) * mm, "mid": v(24.37, -3.74) * mm, "end": v(24.6, -3.18) * mm});
            skPoint(sketch, "E13.25.23.0", {"position": v(24.6, -3.97) * mm});
            skArc(sketch, "E13.26.23.0", {"start": v(23.02, -3.18) * mm, "mid": v(23.25, -3.74) * mm, "end": v(23.81, -3.97) * mm});
            skPoint(sketch, "E13.30.23.0", {"position": v(23.02, 3.97) * mm});
            skPoint(sketch, "E13.31.23.0", {"position": v(23.81, 0) * mm});
            skPoint(sketch, "E13.32.23.0", {"position": v(23.02, -3.97) * mm});
            skLineSegment(sketch, "E14.0.24.0", {"start": v(20.64, -3.97) * mm, "end": v(20.64, -3.97) * mm});
            skPoint(sketch, "E14.3.24.0", {"position": v(21.43, 3.97) * mm});
            skLineSegment(sketch, "E14.4.24.0", {"start": v(20.64, 3.97) * mm, "end": v(20.64, 3.97) * mm});
            skLineSegment(sketch, "E14.7.24.0", {"start": v(19.84, -3.18) * mm, "end": v(19.84, 3.17) * mm});
            skLineSegment(sketch, "E14.10.24.0", {"start": v(21.43, -3.18) * mm, "end": v(21.43, 3.17) * mm});
            skArc(sketch, "E14.13.24.0", {"start": v(20.64, 3.97) * mm, "mid": v(20.08, 3.74) * mm, "end": v(19.84, 3.17) * mm});
            skArc(sketch, "E14.17.24.0", {"start": v(21.43, 3.17) * mm, "mid": v(21.2, 3.74) * mm, "end": v(20.64, 3.97) * mm});
            skArc(sketch, "E14.21.24.0", {"start": v(20.64, -3.97) * mm, "mid": v(21.2, -3.74) * mm, "end": v(21.43, -3.18) * mm});
            skPoint(sketch, "E14.25.24.0", {"position": v(21.43, -3.97) * mm});
            skArc(sketch, "E14.26.24.0", {"start": v(19.84, -3.18) * mm, "mid": v(20.08, -3.74) * mm, "end": v(20.64, -3.97) * mm});
            skPoint(sketch, "E14.30.24.0", {"position": v(19.84, 3.97) * mm});
            skPoint(sketch, "E14.31.24.0", {"position": v(20.64, 0) * mm});
            skPoint(sketch, "E14.32.24.0", {"position": v(19.84, -3.97) * mm});
            skLineSegment(sketch, "E14.0.25.0", {"start": v(17.46, -3.97) * mm, "end": v(17.46, -3.97) * mm});
            skPoint(sketch, "E14.3.25.0", {"position": v(18.26, 3.97) * mm});
            skLineSegment(sketch, "E14.4.25.0", {"start": v(17.46, 3.97) * mm, "end": v(17.46, 3.97) * mm});
            skLineSegment(sketch, "E14.7.25.0", {"start": v(16.67, -3.18) * mm, "end": v(16.67, 3.17) * mm});
            skLineSegment(sketch, "E14.10.25.0", {"start": v(18.26, -3.18) * mm, "end": v(18.26, 3.17) * mm});
            skArc(sketch, "E14.13.25.0", {"start": v(17.46, 3.97) * mm, "mid": v(16.9, 3.74) * mm, "end": v(16.67, 3.17) * mm});
            skArc(sketch, "E14.17.25.0", {"start": v(18.26, 3.17) * mm, "mid": v(18.02, 3.74) * mm, "end": v(17.46, 3.97) * mm});
            skArc(sketch, "E14.21.25.0", {"start": v(17.46, -3.97) * mm, "mid": v(18.02, -3.74) * mm, "end": v(18.26, -3.18) * mm});
            skPoint(sketch, "E14.25.25.0", {"position": v(18.26, -3.97) * mm});
            skArc(sketch, "E14.26.25.0", {"start": v(16.67, -3.18) * mm, "mid": v(16.9, -3.74) * mm, "end": v(17.46, -3.97) * mm});
            skPoint(sketch, "E14.30.25.0", {"position": v(16.67, 3.97) * mm});
            skPoint(sketch, "E14.31.25.0", {"position": v(17.46, 0) * mm});
            skPoint(sketch, "E14.32.25.0", {"position": v(16.67, -3.97) * mm});
            skSolve(sketch);
        }
        {
            var Q0;
            Q0=makeQuery(id+"F9.imprint","IMPRINT",FACE,{"disambiguationData":[TD([[makeQuery(id+"F9.imprint","IMPRINT",EDGE,{"derivedFrom":sQuery(id+"F9.wireOp",EDGE,"E11.2.0.3")}),-1.0]])]});
            var Q1;
            Q1=makeQuery(id+"F9.imprint","IMPRINT",FACE,{"disambiguationData":[TD([[makeQuery(id+"F9.imprint","IMPRINT",EDGE,{"derivedFrom":sQuery(id+"F9.wireOp",EDGE,"E11.3.0.3")}),-1.0]])]});
            var Q2;
            Q2=makeQuery(id+"F9.imprint","IMPRINT",FACE,{"disambiguationData":[TD([[makeQuery(id+"F9.imprint","IMPRINT",EDGE,{"derivedFrom":sQuery(id+"F9.wireOp",EDGE,"E11.4.0.3")}),-1.0]])]});
            var Q3;
            Q3=makeQuery(id+"F9.imprint","IMPRINT",FACE,{"disambiguationData":[TD([[makeQuery(id+"F9.imprint","IMPRINT",EDGE,{"derivedFrom":sQuery(id+"F9.wireOp",EDGE,"E11.5.0.3")}),-1.0]])]});
            var Q4;
            Q4=makeQuery(id+"F9.imprint","IMPRINT",FACE,{"disambiguationData":[TD([[makeQuery(id+"F9.imprint","IMPRINT",EDGE,{"derivedFrom":sQuery(id+"F9.wireOp",EDGE,"E11.6.0.3")}),-1.0]])]});
            var Q5;
            Q5=makeQuery(id+"F9.imprint","IMPRINT",FACE,{"disambiguationData":[TD([[makeQuery(id+"F9.imprint","IMPRINT",EDGE,{"derivedFrom":sQuery(id+"F9.wireOp",EDGE,"E11.7.0.3")}),-1.0]])]});
            var Q6;
            Q6=makeQuery(id+"F9.imprint","IMPRINT",FACE,{"disambiguationData":[TD([[makeQuery(id+"F9.imprint","IMPRINT",EDGE,{"derivedFrom":sQuery(id+"F9.wireOp",EDGE,"E11.8.0.3")}),-1.0]])]});
            var Q7;
            Q7=makeQuery(id+"F9.imprint","IMPRINT",FACE,{"disambiguationData":[TD([[makeQuery(id+"F9.imprint","IMPRINT",EDGE,{"derivedFrom":sQuery(id+"F9.wireOp",EDGE,"E11.9.0.3")}),-1.0]])]});
            var Q8;
            Q8=makeQuery(id+"F9.imprint","IMPRINT",FACE,{"disambiguationData":[TD([[makeQuery(id+"F9.imprint","IMPRINT",EDGE,{"derivedFrom":sQuery(id+"F9.wireOp",EDGE,"E11.10.0.3")}),-1.0]])]});
            var Q9;
            Q9=makeQuery(id+"F9.imprint","IMPRINT",FACE,{"disambiguationData":[TD([[makeQuery(id+"F9.imprint","IMPRINT",EDGE,{"derivedFrom":sQuery(id+"F9.wireOp",EDGE,"E11.11.0.3")}),-1.0]])]});
            var Q10;
            Q10=makeQuery(id+"F9.imprint","IMPRINT",FACE,{"disambiguationData":[TD([[makeQuery(id+"F9.imprint","IMPRINT",EDGE,{"derivedFrom":sQuery(id+"F9.wireOp",EDGE,"E12.7.12.0")}),-1.0]])]});
            var Q11;
            Q11=makeQuery(id+"F9.imprint","IMPRINT",FACE,{"disambiguationData":[TD([[makeQuery(id+"F9.imprint","IMPRINT",EDGE,{"derivedFrom":sQuery(id+"F9.wireOp",EDGE,"E13.7.23.0")}),-1.0]])]});
            var Q12;
            Q12=makeQuery(id+"F9.imprint","IMPRINT",FACE,{"disambiguationData":[TD([[makeQuery(id+"F9.imprint","IMPRINT",EDGE,{"derivedFrom":sQuery(id+"F9.wireOp",EDGE,"E13.7.22.0")}),-1.0]])]});
            var Q13;
            Q13=makeQuery(id+"F9.imprint","IMPRINT",FACE,{"disambiguationData":[TD([[makeQuery(id+"F9.imprint","IMPRINT",EDGE,{"derivedFrom":sQuery(id+"F9.wireOp",EDGE,"E14.7.24.0")}),-1.0]])]});
            var Q14;
            Q14=makeQuery(id+"F9.imprint","IMPRINT",FACE,{"disambiguationData":[TD([[makeQuery(id+"F9.imprint","IMPRINT",EDGE,{"derivedFrom":sQuery(id+"F9.wireOp",EDGE,"E14.7.25.0")}),-1.0]])]});
            var Q15;
            Q15=makeQuery(id+"F9.imprint","IMPRINT",FACE,{"disambiguationData":[TD([[makeQuery(id+"F9.imprint","IMPRINT",EDGE,{"derivedFrom":sQuery(id+"F9.wireOp",EDGE,"E12.7.15.0")}),-1.0]])]});
            var Q16;
            Q16=makeQuery(id+"F9.imprint","IMPRINT",FACE,{"disambiguationData":[TD([[makeQuery(id+"F9.imprint","IMPRINT",EDGE,{"derivedFrom":sQuery(id+"F9.wireOp",EDGE,"E12.7.13.0")}),-1.0]])]});
            var Q17;
            Q17=makeQuery(id+"F9.imprint","IMPRINT",FACE,{"disambiguationData":[TD([[makeQuery(id+"F9.imprint","IMPRINT",EDGE,{"derivedFrom":sQuery(id+"F9.wireOp",EDGE,"E12.7.14.0")}),-1.0]])]});
            var Q18;
            Q18=makeQuery(id+"F9.imprint","IMPRINT",FACE,{"disambiguationData":[TD([[makeQuery(id+"F9.imprint","IMPRINT",EDGE,{"derivedFrom":sQuery(id+"F9.wireOp",EDGE,"E13.7.20.0")}),-1.0]])]});
            var Q19;
            Q19=makeQuery(id+"F9.imprint","IMPRINT",FACE,{"disambiguationData":[TD([[makeQuery(id+"F9.imprint","IMPRINT",EDGE,{"derivedFrom":sQuery(id+"F9.wireOp",EDGE,"E13.7.21.0")}),-1.0]])]});
            var Q20;
            Q20=makeQuery(id+"F9.imprint","IMPRINT",FACE,{"disambiguationData":[TD([[makeQuery(id+"F9.imprint","IMPRINT",EDGE,{"derivedFrom":sQuery(id+"F9.wireOp",EDGE,"E13.7.18.0")}),-1.0]])]});
            var Q21;
            Q21=makeQuery(id+"F9.imprint","IMPRINT",FACE,{"disambiguationData":[TD([[makeQuery(id+"F9.imprint","IMPRINT",EDGE,{"derivedFrom":sQuery(id+"F9.wireOp",EDGE,"E13.7.19.0")}),-1.0]])]});
            var Q22;
            Q22=makeQuery(id+"F9.imprint","IMPRINT",FACE,{"disambiguationData":[TD([[makeQuery(id+"F9.imprint","IMPRINT",EDGE,{"derivedFrom":sQuery(id+"F9.wireOp",EDGE,"E13.7.17.0")}),-1.0]])]});
            var Q23;
            Q23=makeQuery(id+"F9.imprint","IMPRINT",FACE,{"disambiguationData":[TD([[makeQuery(id+"F9.imprint","IMPRINT",EDGE,{"derivedFrom":sQuery(id+"F9.wireOp",EDGE,"E13.7.16.0")}),-1.0]])]});
            var Q24;
            Q24=makeQuery(id+"F9.imprint","IMPRINT",FACE,{"disambiguationData":[TD([[makeQuery(id+"F9.imprint","IMPRINT",EDGE,{"derivedFrom":sQuery(id+"F9.wireOp",EDGE,"E6.left")}),-1.0]])]});
            var Q25;
            Q25=makeQuery(id+"F9.imprint","IMPRINT",FACE,{"disambiguationData":[TD([[makeQuery(id+"F9.imprint","IMPRINT",EDGE,{"derivedFrom":sQuery(id+"F9.wireOp",EDGE,"E11.1.0.3")}),-1.0]])]});
            extrude(context, id + "F10", {"entities" : qUnion([Q0, Q1, Q2, Q3, Q4, Q5, Q6, Q7, Q8, Q9, Q10, Q11, Q12, Q13, Q14, Q15, Q16, Q17, Q18, Q19, Q20, Q21, Q22, Q23, Q24, Q25]), "operationType" : NewBodyOperationType.REMOVE, "endBound" : BoundingType.THROUGH_ALL, "oppositeDirection" : true, "depth" : 25.4 * mm, "offsetDistance" : 25.4 * mm, "hasSecondDirection" : true, "secondDirectionBound" : SecondDirectionBoundingType.THROUGH_ALL, "secondDirectionOppositeDirection" : false, "secondDirectionDepth" : 25.4 * mm});
        }
    });
